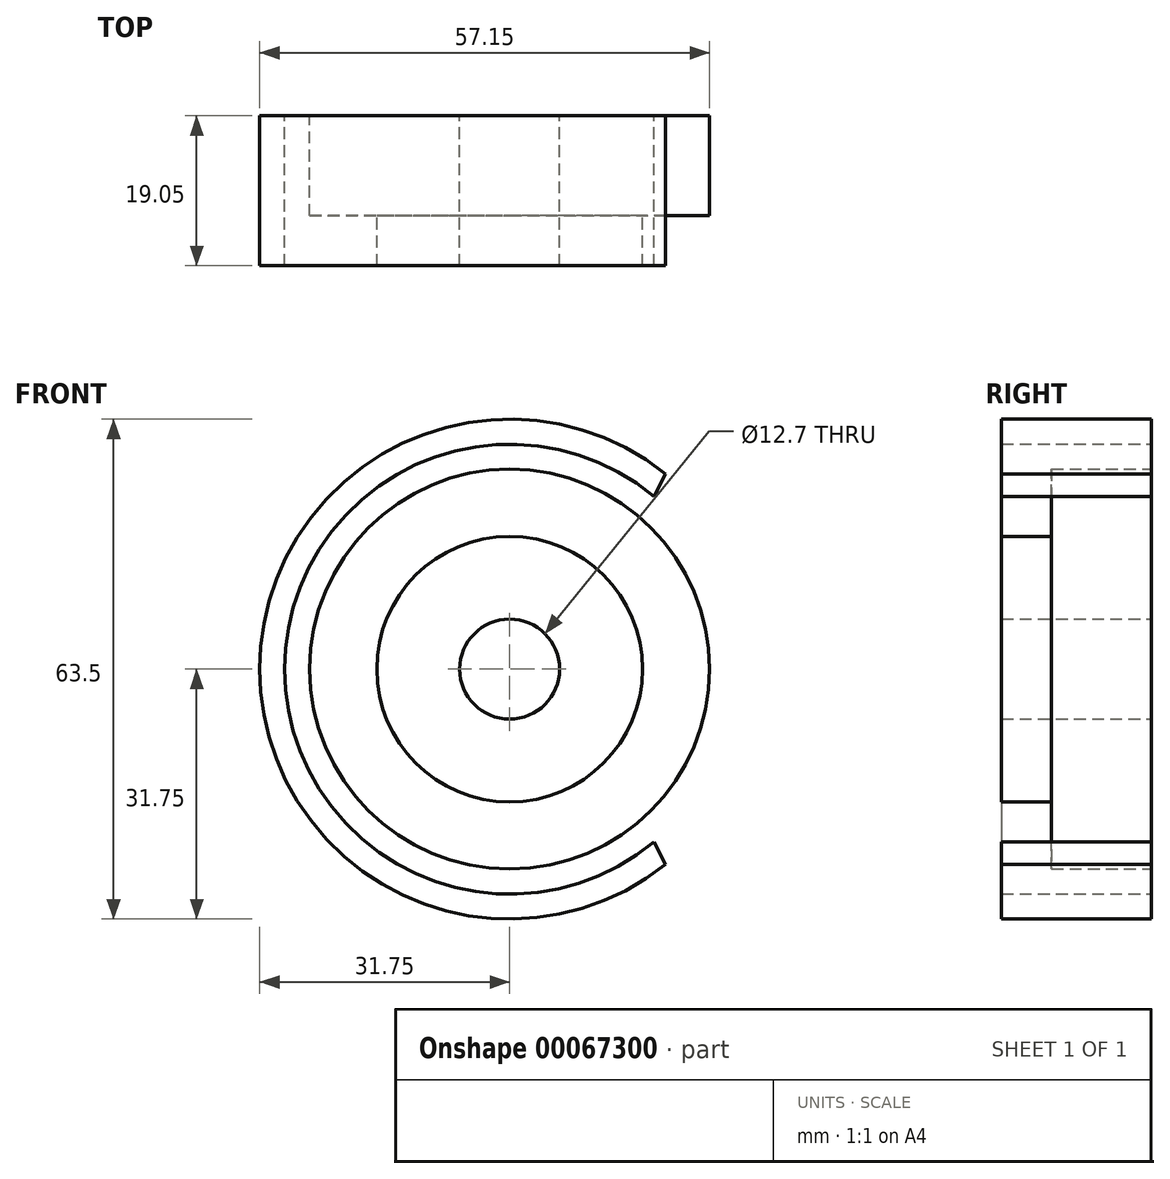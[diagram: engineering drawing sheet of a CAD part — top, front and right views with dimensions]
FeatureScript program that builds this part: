
annotation { "Feature Type Name" : "Feature", "Feature Type Description" : "" }
export const myFeature = defineFeature(function(context is Context, id is Id, definition is map)
    precondition{}
    {
        {
            var Q0;
            Q0=qCreatedBy(makeId("Front.planeOp"),FACE);
            var sketch = newSketch(context, id + "F0", { "sketchPlane" : qUnion([Q0])});
            skCircle(sketch, "E0", {"center": v(0, 0) * mm, "radius": 25.4 * mm});
            skCircle(sketch, "E1", {"center": v(0, 0) * mm, "radius": 6.35 * mm});
            skCircle(sketch, "E2", {"center": v(0, 0) * mm, "radius": 16.87 * mm});
            skSolve(sketch);
        }
        {
            var Q0;
            Q0=makeQuery(id+"F0.imprint","IMPRINT",FACE,{"disambiguationData":[TD([[makeQuery(id+"F0.imprint","IMPRINT",EDGE,{"derivedFrom":sQuery(id+"F0.wireOp",EDGE,"E0")}),1.0]])]});
            extrude(context, id + "F1", {"entities" : qUnion([Q0]), "depth" : 12.7 * mm});
        }
        {
            var Q0;
            Q0=makeQuery(id+"F0.imprint","IMPRINT",FACE,{"disambiguationData":[TD([[makeQuery(id+"F0.imprint","IMPRINT",EDGE,{"derivedFrom":sQuery(id+"F0.wireOp",EDGE,"E1")}),-1.0]])]});
            extrude(context, id + "F2", {"entities" : qUnion([Q0]), "operationType" : NewBodyOperationType.ADD, "depth" : 19.05 * mm});
        }
        {
            var Q0;
            Q0=qCreatedBy(makeId("Front.planeOp"),FACE);
            var sketch = newSketch(context, id + "F3", { "sketchPlane" : qUnion([Q0])});
            skCircle(sketch, "E3.0", {"center": v(0, 0) * mm, "radius": 25.4 * mm});
            skArc(sketch, "E4", {"start": v(18.32, 21.93) * mm, "mid": v(-28.57, 0) * mm, "end": v(18.32, -21.93) * mm});
            skArc(sketch, "E5.0", {"start": v(19.82, 24.8) * mm, "mid": v(-31.75, 0) * mm, "end": v(19.82, -24.8) * mm});
            skLineSegment(sketch, "E6", {"start": v(19.82, 24.8) * mm, "end": v(18.32, 21.93) * mm});
            skLineSegment(sketch, "E7", {"start": v(18.32, -21.93) * mm, "end": v(19.82, -24.8) * mm});
            skLineSegment(sketch, "E8", {"start": v(18.32, 21.93) * mm, "end": v(18.32, -21.93) * mm, "construction": true});
            skLineSegment(sketch, "E9", {"start": v(19.82, 24.8) * mm, "end": v(19.82, -24.8) * mm, "construction": true});
            skSolve(sketch);
        }
        {
            var Q0;
            Q0=makeQuery(id+"F3.imprint","IMPRINT",FACE,{"disambiguationData":[TD([[makeQuery(id+"F3.imprint","IMPRINT",EDGE,{"derivedFrom":sQuery(id+"F3.wireOp",EDGE,"E4")}),-1.0]])]});
            extrude(context, id + "F4", {"entities" : qUnion([Q0]), "depth" : 19.05 * mm});
        }
    });
